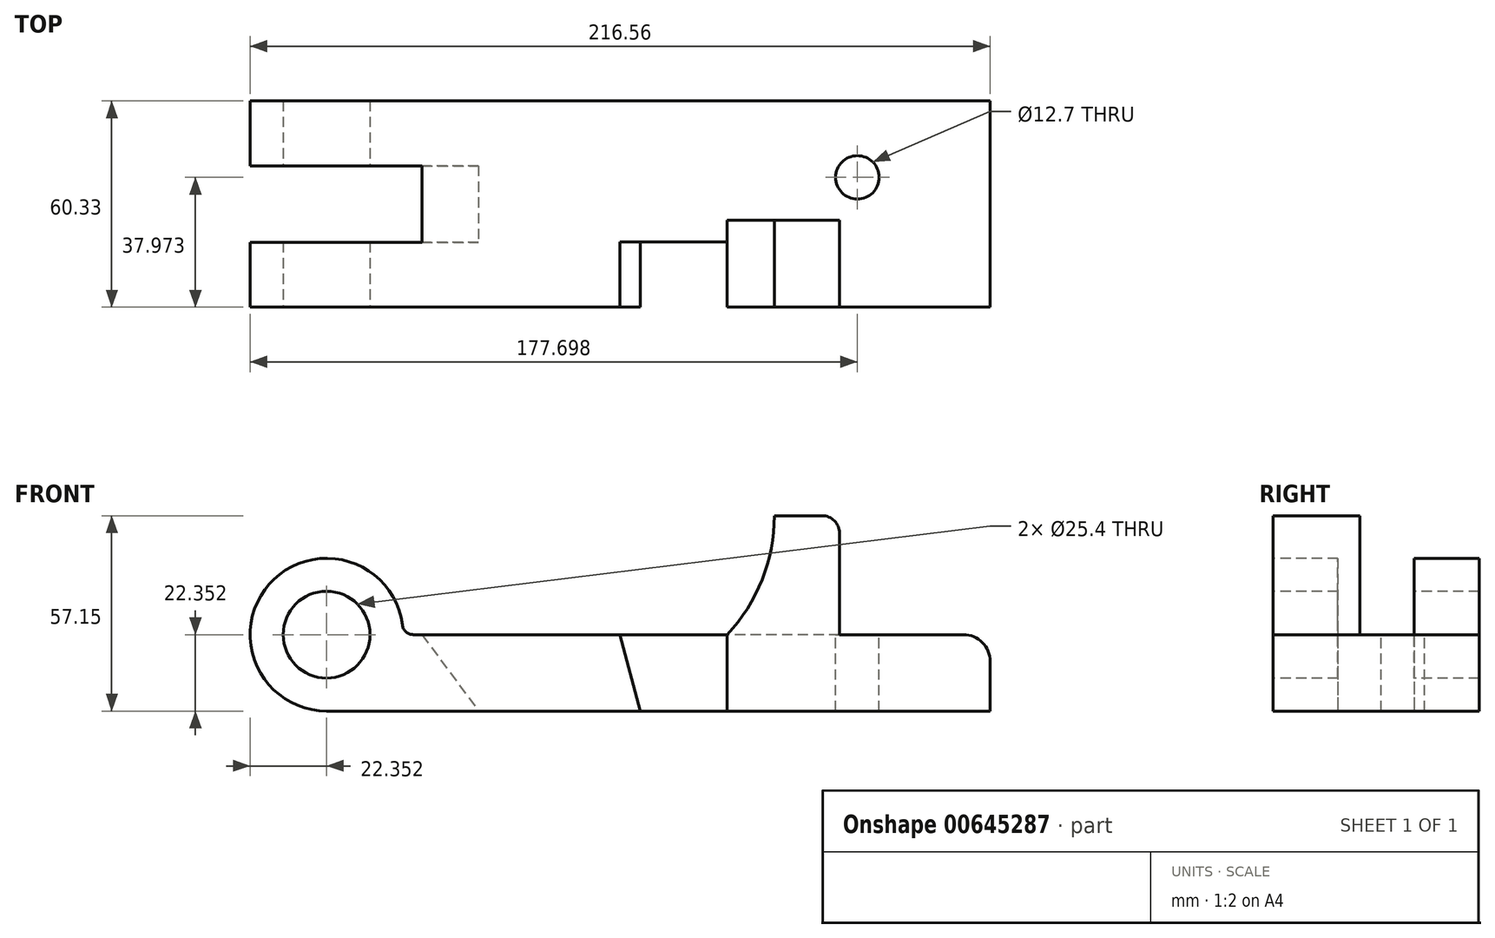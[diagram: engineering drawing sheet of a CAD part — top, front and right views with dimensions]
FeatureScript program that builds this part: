
annotation { "Feature Type Name" : "Feature", "Feature Type Description" : "" }
export const myFeature = defineFeature(function(context is Context, id is Id, definition is map)
    precondition{}
    {
        {
            var Q0;
            Q0=qCreatedBy(makeId("Front.planeOp"),FACE);
            var sketch = newSketch(context, id + "F0", { "sketchPlane" : qUnion([Q0])});
            skLineSegment(sketch, "E0.bottom", {"start": v(0, 0) * mm, "end": v(-194.2, 0) * mm});
            skLineSegment(sketch, "E0.top", {"start": v(0, 22.35) * mm, "end": v(-194.2, 22.35) * mm});
            skLineSegment(sketch, "E0.left", {"start": v(0, 0) * mm, "end": v(0, 22.35) * mm});
            skLineSegment(sketch, "E0.right", {"start": v(-194.2, 0) * mm, "end": v(-194.2, 22.35) * mm});
            skCircle(sketch, "E1", {"center": v(-194.2, 22.35) * mm, "radius": 22.35 * mm});
            skCircle(sketch, "E2", {"center": v(-194.2, 22.35) * mm, "radius": 12.7 * mm});
            skLineSegment(sketch, "E3", {"start": v(-44.12, 22.35) * mm, "end": v(-44.12, 52.07) * mm});
            skLineSegment(sketch, "E4", {"start": v(-49.2, 57.15) * mm, "end": v(-63.17, 57.15) * mm});
            skLineSegment(sketch, "E5", {"start": v(-76.96, 0) * mm, "end": v(-76.96, 22.35) * mm});
            skArc(sketch, "E6", {"start": v(-76.96, 22.35) * mm, "mid": v(-66.74, 38.43) * mm, "end": v(-63.17, 57.15) * mm});
            skPoint(sketch, "E7.visualSharp", {"position": v(-44.12, 57.15) * mm});
            skArc(sketch, "E7.filletArc", {"start": v(-44.12, 52.07) * mm, "mid": v(-45.6, 55.66) * mm, "end": v(-49.2, 57.15) * mm});
            skLineSegment(sketch, "E8", {"start": v(-102.36, 0) * mm, "end": v(-108.36, 22.35) * mm});
            skLineSegment(sketch, "E9", {"start": v(-166.27, 22.35) * mm, "end": v(-149.76, 0) * mm});
            skSolve(sketch);
        }
        {
            var Q0;
            {var subQ0=sQuery(id+"F0.wireOp",EDGE,"E1");var subQ1=sQuery(id+"F0.wireOp",EDGE,"E0.top");var subQ2=makeQuery(id+"F0.imprint","INTERSECT",VERTEX,{"derivedFrom":[subQ1,subQ0]});Q0=makeQuery(id+"F0.imprint","IMPRINT",FACE,{"disambiguationData":[TD([[makeQuery(id+"F0.imprint","IMPRINT",EDGE,{"disambiguationData":[TD([[subQ2,-1.0]])],"derivedFrom":subQ1}),-1.0]])]});}
            var Q1;
            {var subQ0=sQuery(id+"F0.wireOp",EDGE,"E1");var subQ1=sQuery(id+"F0.wireOp",EDGE,"E0.top");var subQ2=makeQuery(id+"F0.imprint","INTERSECT",VERTEX,{"derivedFrom":[subQ1,subQ0]});Q1=makeQuery(id+"F0.imprint","IMPRINT",FACE,{"disambiguationData":[TD([[makeQuery(id+"F0.imprint","IMPRINT",EDGE,{"disambiguationData":[TD([[subQ2,-1.0]])],"derivedFrom":subQ1}),1.0]])]});}
            var Q2;
            {var subQ3=sQuery(id+"F0.wireOp",EDGE,"E9");Q2=makeQuery(id+"F0.imprint","IMPRINT",FACE,{"disambiguationData":[TD([[makeQuery(id+"F0.imprint","IMPRINT",EDGE,{"derivedFrom":subQ3}),-1.0]])]});}
            var Q3;
            {var subQ0=sQuery(id+"F0.wireOp",EDGE,"E8");Q3=makeQuery(id+"F0.imprint","IMPRINT",FACE,{"disambiguationData":[TD([[makeQuery(id+"F0.imprint","IMPRINT",EDGE,{"derivedFrom":subQ0}),1.0]])]});}
            extrude(context, id + "F1", {"entities" : qUnion([Q0, Q1, Q2, Q3]), "oppositeDirection" : true, "depth" : 19 * mm, "offsetDistance" : 25.4 * mm});
        }
        {
            var Q0;
            {var subQ0=sQuery(id+"F0.wireOp",EDGE,"E1");var subQ1=sQuery(id+"F0.wireOp",EDGE,"E0.top");var subQ2=makeQuery(id+"F0.imprint","INTERSECT",VERTEX,{"derivedFrom":[subQ1,subQ0]});Q0=makeQuery(id+"F0.imprint","IMPRINT",FACE,{"disambiguationData":[TD([[makeQuery(id+"F0.imprint","IMPRINT",EDGE,{"disambiguationData":[TD([[subQ2,-1.0]])],"derivedFrom":subQ1}),-1.0]])]});}
            var Q1;
            {var subQ3=sQuery(id+"F0.wireOp",EDGE,"E9");Q1=makeQuery(id+"F0.imprint","IMPRINT",FACE,{"disambiguationData":[TD([[makeQuery(id+"F0.imprint","IMPRINT",EDGE,{"derivedFrom":subQ3}),-1.0]])]});}
            var Q2;
            {var subQ0=sQuery(id+"F0.wireOp",EDGE,"E1");var subQ1=sQuery(id+"F0.wireOp",EDGE,"E0.top");var subQ2=makeQuery(id+"F0.imprint","INTERSECT",VERTEX,{"derivedFrom":[subQ1,subQ0]});Q2=makeQuery(id+"F0.imprint","IMPRINT",FACE,{"disambiguationData":[TD([[makeQuery(id+"F0.imprint","IMPRINT",EDGE,{"disambiguationData":[TD([[subQ2,-1.0]])],"derivedFrom":subQ1}),1.0]])]});}
            var Q3;
            {var subQ0=sQuery(id+"F0.wireOp",EDGE,"E8");Q3=makeQuery(id+"F0.imprint","IMPRINT",FACE,{"disambiguationData":[TD([[makeQuery(id+"F0.imprint","IMPRINT",EDGE,{"derivedFrom":subQ0}),1.0]])]});}
            extrude(context, id + "F2", {"entities" : qUnion([Q0, Q1, Q2, Q3]), "oppositeDirection" : true, "depth" : 60.32 * mm, "offsetDistance" : 25.4 * mm, "hasSecondDirection" : true, "secondDirectionOppositeDirection" : true, "secondDirectionDepth" : 41.33 * mm});
        }
        {
            var Q0;
            {var subQ0=sQuery(id+"F0.wireOp",EDGE,"E8");Q0=makeQuery(id+"F0.imprint","IMPRINT",FACE,{"disambiguationData":[TD([[makeQuery(id+"F0.imprint","IMPRINT",EDGE,{"derivedFrom":subQ0}),1.0]])]});}
            var Q1;
            Q1=makeQuery(id+"F2.opExtrude","CAP_FACE",FACE,{"disambiguationData":[OSD([sQuery(id+"F0.wireOp",EDGE,"E0.bottom"),sQuery(id+"F0.wireOp",EDGE,"E0.top"),sQuery(id+"F0.wireOp",EDGE,"E1"),sQuery(id+"F0.wireOp",EDGE,"E2"),sQuery(id+"F0.wireOp",EDGE,"E8")])],"isStart":false});
            extrude(context, id + "F3", {"entities" : qUnion([Q0]), "operationType" : NewBodyOperationType.ADD, "endBound" : BoundingType.UP_TO_SURFACE, "oppositeDirection" : true, "depth" : 25.4 * mm, "endBoundEntityFace" : qUnion([Q1]), "offsetDistance" : 25.4 * mm});
        }
        {
            var Q0;
            {var subQ0=sQuery(id+"F0.wireOp",EDGE,"E0.left");Q0=makeQuery(id+"F0.imprint","IMPRINT",FACE,{"disambiguationData":[TD([[makeQuery(id+"F0.imprint","IMPRINT",EDGE,{"derivedFrom":subQ0}),1.0]])]});}
            extrude(context, id + "F4", {"entities" : qUnion([Q0]), "oppositeDirection" : true, "depth" : 60.32 * mm, "offsetDistance" : 25.4 * mm});
        }
        {
            var Q0;
            {var subQ0=sQuery(id+"F0.wireOp",EDGE,"E5");Q0=makeQuery(id+"F0.imprint","IMPRINT",FACE,{"disambiguationData":[TD([[makeQuery(id+"F0.imprint","IMPRINT",EDGE,{"derivedFrom":subQ0}),1.0]])]});}
            extrude(context, id + "F5", {"entities" : qUnion([Q0]), "operationType" : NewBodyOperationType.ADD, "oppositeDirection" : true, "depth" : 60.32 * mm, "offsetDistance" : 25.4 * mm, "hasSecondDirection" : true, "secondDirectionOppositeDirection" : true, "secondDirectionDepth" : 19.05 * mm});
        }
        {
            var Q0;
            {var subQ1=sQuery(id+"F0.wireOp",EDGE,"E3");Q0=makeQuery(id+"F0.imprint","IMPRINT",FACE,{"disambiguationData":[TD([[makeQuery(id+"F0.imprint","IMPRINT",EDGE,{"derivedFrom":subQ1}),1.0]])]});}
            extrude(context, id + "F6", {"entities" : qUnion([Q0]), "operationType" : NewBodyOperationType.ADD, "oppositeDirection" : true, "depth" : 25.4 * mm, "offsetDistance" : 25.4 * mm});
        }
        {
            var Q0;
            Q0=makeQuery(id+"F6.opExtrude","SWEPT_EDGE",EDGE,{"disambiguationData":[OSD([sQuery(id+"F0.wireOp",EDGE,"E0.top"),sQuery(id+"F0.wireOp",EDGE,"E3")])]});
            var Q1;
            Q1=makeQuery(id+"F1.opExtrude","SWEPT_EDGE",EDGE,{"disambiguationData":[OSD([sQuery(id+"F0.wireOp",EDGE,"E0.top"),sQuery(id+"F0.wireOp",EDGE,"E1")])]});
            var Q2;
            Q2=makeQuery(id+"F2.opExtrude","SWEPT_EDGE",EDGE,{"disambiguationData":[OSD([sQuery(id+"F0.wireOp",EDGE,"E0.top"),sQuery(id+"F0.wireOp",EDGE,"E1")])]});
            fillet(context, id + "F7", {"entities" : qUnion([Q0, Q1, Q2]), "radius" : 3.3 * mm, "tangentPropagation" : true, "allowEdgeOverflow" : false});
        }
        {
            var Q0;
            Q0=makeQuery(id+"F4.opExtrude","SWEPT_EDGE",EDGE,{"disambiguationData":[OSD([sQuery(id+"F0.wireOp",EDGE,"E0.top"),sQuery(id+"F0.wireOp",EDGE,"E0.left")])]});
            fillet(context, id + "F8", {"entities" : qUnion([Q0]), "radius" : 7.87 * mm, "tangentPropagation" : true, "allowEdgeOverflow" : false});
        }
        {
            var Q0;
            {var subQ0=sQuery(id+"F0.wireOp",EDGE,"E0.top");Q0=makeQuery(id+"F5.boolean.opBoolean","MERGE",FACE,{"derivedFrom":[makeQuery(id+"F3.boolean.opBoolean","MERGE",FACE,{"derivedFrom":[makeQuery(id+"F1.opExtrude","SWEPT_FACE",FACE,{"disambiguationData":[OSD([subQ0])]}),makeQuery(id+"F2.opExtrude","SWEPT_FACE",FACE,{"disambiguationData":[OSD([subQ0])]}),makeQuery(id+"F3.opExtrude","SWEPT_FACE",FACE,{"disambiguationData":[OSD([subQ0])]})]}),makeQuery(id+"F4.opExtrude","SWEPT_FACE",FACE,{"disambiguationData":[OSD([subQ0])]}),makeQuery(id+"F5.opExtrude","SWEPT_FACE",FACE,{"disambiguationData":[OSD([subQ0])]})]});}
            var sketch = newSketch(context, id + "F9", { "sketchPlane" : qUnion([Q0])});
            skCircle(sketch, "E10", {"center": v(-38.86, 37.97) * mm, "radius": 6.35 * mm});
            skSolve(sketch);
        }
        {
            var Q0;
            Q0=makeQuery(id+"F9.imprint","IMPRINT",FACE,{"disambiguationData":[TD([[makeQuery(id+"F9.imprint","IMPRINT",EDGE,{"derivedFrom":sQuery(id+"F9.wireOp",EDGE,"E10")}),1.0]])]});
            extrude(context, id + "F10", {"entities" : qUnion([Q0]), "operationType" : NewBodyOperationType.REMOVE, "endBound" : BoundingType.THROUGH_ALL, "oppositeDirection" : true, "depth" : 25.4 * mm, "offsetDistance" : 25.4 * mm});
        }
    });
